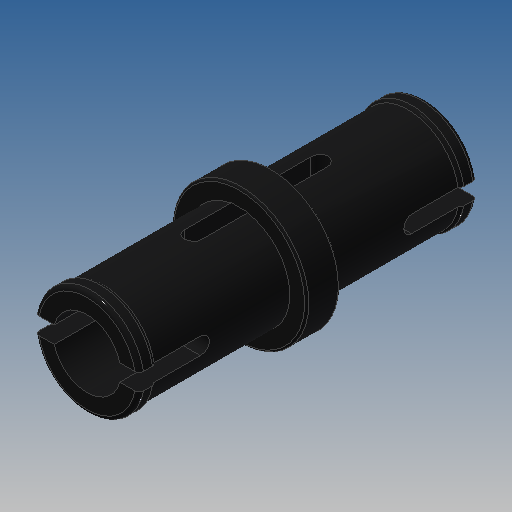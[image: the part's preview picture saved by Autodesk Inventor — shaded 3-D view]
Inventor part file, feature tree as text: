
AUTODESK INVENTOR PART (.ipt)
format: ipt  version: 2022.2 (Build 262287000, 287)  size: 285,184 bytes
history: native  units: mm (DEFAULTED — no unit token found)
features: sketch x2, extrude x2, revolve x1, fillet x1
ambient origin geometry x8: Origin, YZ Plane, XZ Plane, XY Plane, X Axis, Y Axis, Z Axis, Center Point
bodies: Solid2 (feature_tree)
feature tree (6):
  sketch  "Sketch1"  dims[d1=4.8mm d2=5.0mm d6=8.0mm]
  revolve  "Revolution1"  [1 undecoded]
  fillet  "Fillet1"  Radius=8.0mm
  extrude  "Extrusion1"  Depth=10.0mm
  extrude  "Extrusion2"  Depth=0.8mm
  sketch  "Sketch2"  dims[d7=0.8mm d8=6.4mm d9=0.8mm d10=0.8mm d14=0.8mm d19=8.0mm d20=90.0deg d21=4.8mm d22=0.0mm d24=0.8mm d25=10.0mm d26=0.0mm d27=0.2mm d28=0.1mm d29=0.0mm d30=0.0mm d31=3.4mm d32=3.2mm d33=3.4mm]
note: 1 required parameter value undecoded (feature->parameter linkage not recoverable at this tier; creation-order binding heuristic only, values carry confidence <= 0.55)
